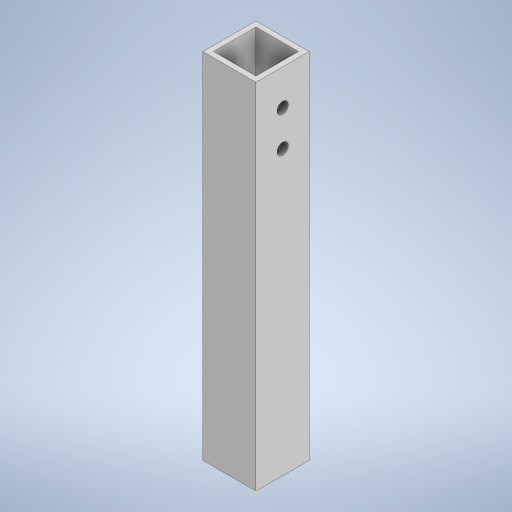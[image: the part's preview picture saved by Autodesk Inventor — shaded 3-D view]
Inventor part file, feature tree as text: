
AUTODESK INVENTOR PART (.ipt)
format: ipt  version: 2023 (Build 270158000, 158)  size: 247,808 bytes
history: native  units: mm
features: sketch x4, extrude x2, other x1, hole x1
ambient origin geometry x8: Origin, YZ Plane, XZ Plane, XY Plane, X Axis, Y Axis, Z Axis, Center Point
bodies: Body1 (feature_tree)
feature tree (8):
  other  "ソリッド1"
  extrude  "押し出し1"  Depth=15.0mm
  extrude  "押し出し2"  Depth=15.0mm
  sketch  "スケッチ3"
  hole  "穴1"  [1 undecoded]
  sketch  "スケッチ1"
  sketch  "スケッチ2"
  sketch  "スケッチ4"
note: 1 required parameter value undecoded (feature->parameter linkage not recoverable at this tier; creation-order binding heuristic only, values carry confidence <= 0.55)
